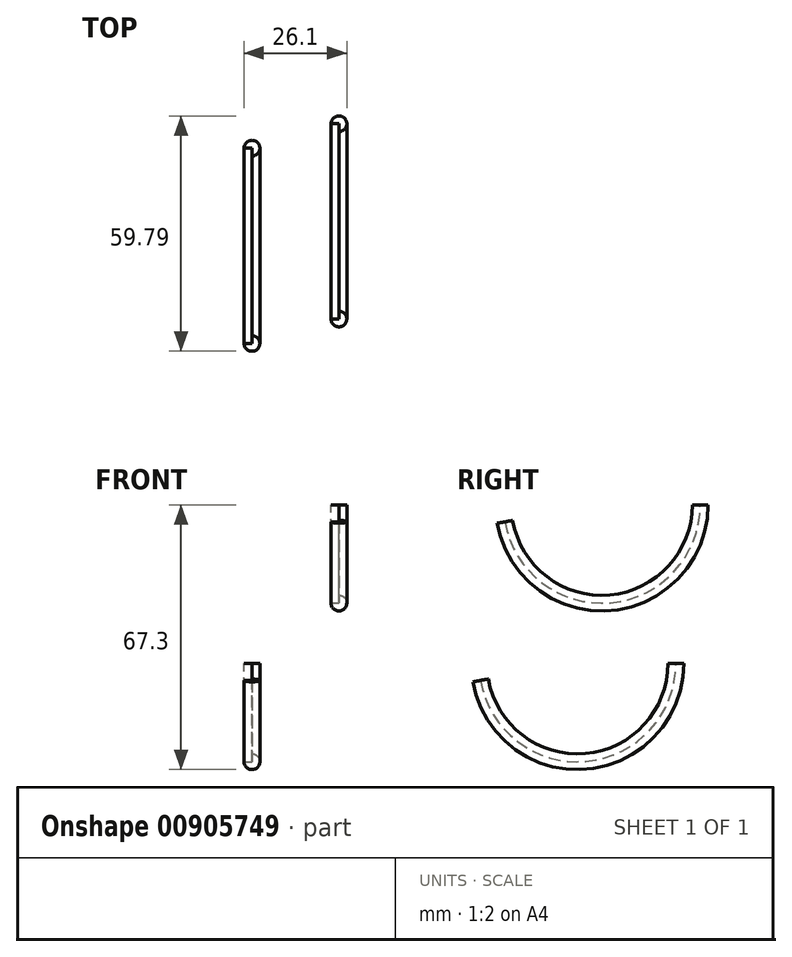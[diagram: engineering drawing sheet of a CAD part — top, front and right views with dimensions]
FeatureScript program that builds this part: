
annotation { "Feature Type Name" : "Feature", "Feature Type Description" : "" }
export const myFeature = defineFeature(function(context is Context, id is Id, definition is map)
    precondition{}
    {
        {
            var Q0;
            Q0=qCreatedBy(makeId("Top.planeOp"),FACE);
            var sketch = newSketch(context, id + "F0", { "sketchPlane" : qUnion([Q0])});
            skLineSegment(sketch, "E0.bottom", {"start": v(0, 0) * mm, "end": v(25, 0) * mm});
            skLineSegment(sketch, "E0.top", {"start": v(0, 25) * mm, "end": v(25, 25) * mm});
            skLineSegment(sketch, "E0.left", {"start": v(0, 0) * mm, "end": v(0, 25) * mm});
            skLineSegment(sketch, "E0.right", {"start": v(25, 0) * mm, "end": v(25, 25) * mm});
            skCircle(sketch, "E1", {"center": v(25, 25) * mm, "radius": 2 * mm});
            skSolve(sketch);
        }
        {
            var Q0;
            {var subQ0=sQuery(id+"F0.wireOp",EDGE,"E0.right");var subQ1=sQuery(id+"F0.wireOp",EDGE,"E0.top");var subQ2=makeQuery(id+"F0.imprint","INTERSECT",VERTEX,{"derivedFrom":[subQ1,subQ0]});Q0=makeQuery(id+"F0.imprint","IMPRINT",FACE,{"disambiguationData":[TD([[makeQuery(id+"F0.imprint","IMPRINT",EDGE,{"disambiguationData":[TD([[subQ2,1.0]])],"derivedFrom":subQ1}),1.0]])]});}
            var Q1;
            Q1=sQuery(id+"F0.wireOp",EDGE,"E0.bottom");
            revolve(context, id + "F1", {"surfaceOperationType" : NewSurfaceOperationType.NEW, "entities" : qUnion([Q0]), "axis" : qUnion([Q1]), "revolveType" : RevolveType.ONE_DIRECTION, "oppositeDirection" : true, "angle" : 170 * degree});
        }
        {
            var Q0;
            Q0=makeQuery(id+"F1.opRevolve","SWEPT_BODY",BODY,{"disambiguationData":[OSD([sQuery(id+"F0.wireOp",EDGE,"E0.top"),sQuery(id+"F0.wireOp",EDGE,"E0.right"),sQuery(id+"F0.wireOp",EDGE,"E1")])]});
            var Q1;
            Q1=makeQuery(id+"F1.opRevolve","SWEPT_EDGE",EDGE,{"disambiguationData":[OSD([sQuery(id+"F0.wireOp",EDGE,"E0.right"),sQuery(id+"F0.wireOp",EDGE,"E1")])]});
            transform(context, id + "F2", {"entities" : qUnion([Q0]), "transformType" : TransformType.TRANSLATION_3D, "dx" : 22.1 * mm, "dy" : 6.2 * mm, "dz" : 40.3 * mm, "makeCopy" : true});
        }
    });
